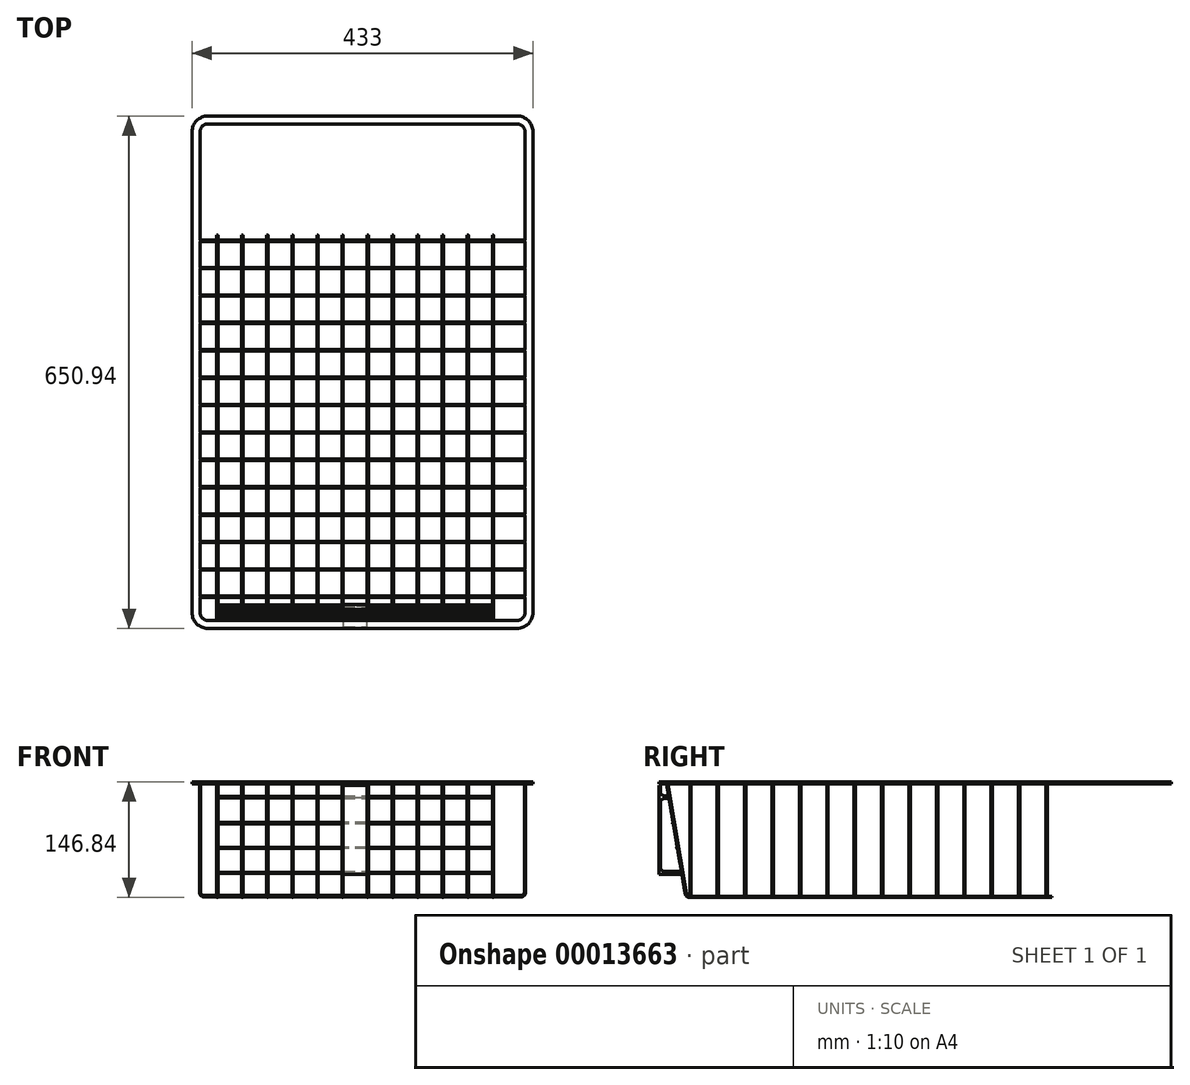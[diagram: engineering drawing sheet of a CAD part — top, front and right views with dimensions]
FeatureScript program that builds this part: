
annotation { "Feature Type Name" : "Feature", "Feature Type Description" : "" }
export const myFeature = defineFeature(function(context is Context, id is Id, definition is map)
    precondition{}
    {
        {
            var Q0;
            Q0=qCreatedBy(makeId("Top.planeOp"),FACE);
            var sketch = newSketch(context, id + "F0", { "sketchPlane" : qUnion([Q0])});
            skCircle(sketch, "E0", {"center": v(-48.63, -32.17) * mm, "radius": 0.85 * mm});
            skCircle(sketch, "E1.0.1.0", {"center": v(-48.63, 2.63) * mm, "radius": 0.85 * mm});
            skCircle(sketch, "E1.0.2.0", {"center": v(-48.63, 37.43) * mm, "radius": 0.85 * mm});
            skCircle(sketch, "E1.0.3.0", {"center": v(-48.63, 72.23) * mm, "radius": 0.85 * mm});
            skCircle(sketch, "E1.0.4.0", {"center": v(-48.63, 107.03) * mm, "radius": 0.85 * mm});
            skCircle(sketch, "E1.0.5.0", {"center": v(-48.63, 141.83) * mm, "radius": 0.85 * mm});
            skCircle(sketch, "E1.0.6.0", {"center": v(-48.63, 176.63) * mm, "radius": 0.85 * mm});
            skCircle(sketch, "E1.0.7.0", {"center": v(-48.63, 211.43) * mm, "radius": 0.85 * mm});
            skCircle(sketch, "E1.0.8.0", {"center": v(-48.63, 246.23) * mm, "radius": 0.85 * mm});
            skCircle(sketch, "E1.0.9.0", {"center": v(-48.63, 281.03) * mm, "radius": 0.85 * mm});
            skCircle(sketch, "E1.0.10.0", {"center": v(-48.63, 315.83) * mm, "radius": 0.85 * mm});
            skCircle(sketch, "E1.0.11.0", {"center": v(-48.63, 350.63) * mm, "radius": 0.85 * mm});
            skCircle(sketch, "E1.0.12.0", {"center": v(-48.63, 385.43) * mm, "radius": 0.85 * mm});
            skCircle(sketch, "E1.0.13.0", {"center": v(-48.63, 420.23) * mm, "radius": 0.85 * mm});
            skLineSegment(sketch, "E1.direction1", {"start": v(-48.63, -32.17) * mm, "end": v(38.17, -32.17) * mm, "construction": true});
            skLineSegment(sketch, "E1.direction2", {"start": v(-48.63, -32.17) * mm, "end": v(-48.63, 2.63) * mm, "construction": true});
            skSolve(sketch);
        }
        {
            var Q0;
            Q0=qCreatedBy(makeId("Front.planeOp"),FACE);
            var sketch = newSketch(context, id + "F1", { "sketchPlane" : qUnion([Q0])});
            skPoint(sketch, "E2.0", {"position": v(-48.63, 0) * mm});
            skLineSegment(sketch, "E3", {"start": v(-48.63, 0) * mm, "end": v(-48.63, -140) * mm});
            skLineSegment(sketch, "E4", {"start": v(-43.63, -145) * mm, "end": v(359.17, -145) * mm});
            skLineSegment(sketch, "E5", {"start": v(364.17, -140) * mm, "end": v(364.17, 0) * mm});
            skPoint(sketch, "E6.visualSharp", {"position": v(-48.63, -145) * mm});
            skArc(sketch, "E6.filletArc", {"start": v(-48.63, -140) * mm, "mid": v(-47.17, -143.54) * mm, "end": v(-43.63, -145) * mm});
            skPoint(sketch, "E7.visualSharp", {"position": v(364.17, -145) * mm});
            skArc(sketch, "E7.filletArc", {"start": v(359.17, -145) * mm, "mid": v(362.7, -143.54) * mm, "end": v(364.17, -140) * mm});
            skCircle(sketch, "E8", {"center": v(-26.63, -145.85) * mm, "radius": 0.85 * mm});
            skLineSegment(sketch, "E9.0", {"start": v(-49.48, 0) * mm, "end": v(-47.78, 0) * mm});
            skCircle(sketch, "E10", {"center": v(-48.63, 0) * mm, "radius": 0.85 * mm, "construction": true});
            skCircle(sketch, "E11.1.0.0", {"center": v(5.2, -145.85) * mm, "radius": 0.85 * mm});
            skCircle(sketch, "E11.2.0.0", {"center": v(37.02, -145.85) * mm, "radius": 0.85 * mm});
            skCircle(sketch, "E11.3.0.0", {"center": v(68.84, -145.85) * mm, "radius": 0.85 * mm});
            skCircle(sketch, "E11.4.0.0", {"center": v(100.67, -145.85) * mm, "radius": 0.85 * mm});
            skCircle(sketch, "E11.5.0.0", {"center": v(132.5, -145.85) * mm, "radius": 0.85 * mm});
            skCircle(sketch, "E11.6.0.0", {"center": v(164.32, -145.85) * mm, "radius": 0.85 * mm});
            skCircle(sketch, "E11.7.0.0", {"center": v(196.14, -145.85) * mm, "radius": 0.85 * mm});
            skCircle(sketch, "E11.8.0.0", {"center": v(227.97, -145.85) * mm, "radius": 0.85 * mm});
            skCircle(sketch, "E11.9.0.0", {"center": v(259.8, -145.85) * mm, "radius": 0.85 * mm});
            skCircle(sketch, "E11.10.0.0", {"center": v(291.62, -145.85) * mm, "radius": 0.85 * mm});
            skCircle(sketch, "E11.11.0.0", {"center": v(323.44, -145.85) * mm, "radius": 0.85 * mm});
            skLineSegment(sketch, "E11.direction1", {"start": v(-26.63, -145.85) * mm, "end": v(5.2, -145.85) * mm, "construction": true});
            skLineSegment(sketch, "E12", {"start": v(-49.48, 0) * mm, "end": v(-49.48, -289.47) * mm, "construction": true});
            skLineSegment(sketch, "E13", {"start": v(133.34, -145) * mm, "end": v(133.34, -145.85) * mm, "construction": true});
            skLineSegment(sketch, "E14", {"start": v(163.47, -145) * mm, "end": v(163.47, -145.85) * mm, "construction": true});
            skSolve(sketch);
        }
        {
            var Q0;
            Q0 = qSketchRegion(id + "F0", true);
            var Q1;
            Q1=sQuery(id+"F1.wireOp",EDGE,"E3");
            var Q2;
            Q2=sQuery(id+"F1.wireOp",EDGE,"E6.filletArc");
            var Q3;
            Q3=sQuery(id+"F1.wireOp",EDGE,"E4");
            var Q4;
            Q4=sQuery(id+"F1.wireOp",EDGE,"E7.filletArc");
            var Q5;
            Q5=sQuery(id+"F1.wireOp",EDGE,"E5");
            sweep(context, id + "F2", {"profiles" : qUnion([Q0]), "path" : qUnion([Q1, Q2, Q3, Q4, Q5])});
        }
        {
            var Q0;
            Q0=qCreatedBy(makeId("Right.planeOp"),FACE);
            var sketch = newSketch(context, id + "F3", { "sketchPlane" : qUnion([Q0])});
            skPoint(sketch, "E15.0", {"position": v(-32.17, 0) * mm});
            skLineSegment(sketch, "E16", {"start": v(-62.17, 0) * mm, "end": v(-38.17, -141.69) * mm});
            skLineSegment(sketch, "E17", {"start": v(-33.24, -145.85) * mm, "end": v(0, -145.85) * mm});
            skPoint(sketch, "E18.visualSharp", {"position": v(-37.46, -145.85) * mm});
            skArc(sketch, "E18.filletArc", {"start": v(-38.17, -141.69) * mm, "mid": v(-36.46, -144.67) * mm, "end": v(-33.24, -145.85) * mm});
            skPoint(sketch, "E19.0", {"position": v(0, -145.85) * mm});
            skCircle(sketch, "E20.0", {"center": v(-32.17, -145) * mm, "radius": 0.85 * mm, "construction": true});
            skLineSegment(sketch, "E21", {"start": v(0, -145.85) * mm, "end": v(427.21, -145.85) * mm});
            skPoint(sketch, "E22", {"position": v(-58.93, -19.08) * mm});
            skLineSegment(sketch, "E23.0", {"start": v(-33.02, 0) * mm, "end": v(-31.32, 0) * mm});
            skCircle(sketch, "E24", {"center": v(-59.77, -19.22) * mm, "radius": 0.85 * mm});
            skLineSegment(sketch, "E25", {"start": v(-31.32, 0) * mm, "end": v(-32.17, 0) * mm, "construction": true});
            skLineSegment(sketch, "E26", {"start": v(-58.93, -19.08) * mm, "end": v(-60.61, -19.36) * mm, "construction": true});
            skLineSegment(sketch, "E27", {"start": v(-63.03, 0) * mm, "end": v(-37.46, -150.94) * mm, "construction": true});
            skCircle(sketch, "E28", {"center": v(-54.17, -52.29) * mm, "radius": 0.85 * mm});
            skCircle(sketch, "E29", {"center": v(-48.86, -83.66) * mm, "radius": 0.85 * mm});
            skCircle(sketch, "E30", {"center": v(-43.47, -115.45) * mm, "radius": 0.85 * mm});
            skSolve(sketch);
        }
        {
            var Q0;
            Q0=makeQuery(id+"F1.imprint","IMPRINT",FACE,{"disambiguationData":[TD([[makeQuery(id+"F1.imprint","IMPRINT",EDGE,{"derivedFrom":sQuery(id+"F1.wireOp",EDGE,"E8")}),1.0]])]});
            var Q1;
            Q1=makeQuery(id+"F1.imprint","IMPRINT",FACE,{"disambiguationData":[TD([[makeQuery(id+"F1.imprint","IMPRINT",EDGE,{"derivedFrom":sQuery(id+"F1.wireOp",EDGE,"E11.1.0.0")}),1.0]])]});
            var Q2;
            Q2=makeQuery(id+"F1.imprint","IMPRINT",FACE,{"disambiguationData":[TD([[makeQuery(id+"F1.imprint","IMPRINT",EDGE,{"derivedFrom":sQuery(id+"F1.wireOp",EDGE,"E11.2.0.0")}),1.0]])]});
            var Q3;
            Q3=makeQuery(id+"F1.imprint","IMPRINT",FACE,{"disambiguationData":[TD([[makeQuery(id+"F1.imprint","IMPRINT",EDGE,{"derivedFrom":sQuery(id+"F1.wireOp",EDGE,"E11.3.0.0")}),1.0]])]});
            var Q4;
            Q4=makeQuery(id+"F1.imprint","IMPRINT",FACE,{"disambiguationData":[TD([[makeQuery(id+"F1.imprint","IMPRINT",EDGE,{"derivedFrom":sQuery(id+"F1.wireOp",EDGE,"E11.4.0.0")}),1.0]])]});
            var Q5;
            Q5=makeQuery(id+"F1.imprint","IMPRINT",FACE,{"disambiguationData":[TD([[makeQuery(id+"F1.imprint","IMPRINT",EDGE,{"derivedFrom":sQuery(id+"F1.wireOp",EDGE,"E11.5.0.0")}),1.0]])]});
            var Q6;
            Q6=makeQuery(id+"F1.imprint","IMPRINT",FACE,{"disambiguationData":[TD([[makeQuery(id+"F1.imprint","IMPRINT",EDGE,{"derivedFrom":sQuery(id+"F1.wireOp",EDGE,"E11.6.0.0")}),1.0]])]});
            var Q7;
            Q7=makeQuery(id+"F1.imprint","IMPRINT",FACE,{"disambiguationData":[TD([[makeQuery(id+"F1.imprint","IMPRINT",EDGE,{"derivedFrom":sQuery(id+"F1.wireOp",EDGE,"E11.7.0.0")}),1.0]])]});
            var Q8;
            Q8=makeQuery(id+"F1.imprint","IMPRINT",FACE,{"disambiguationData":[TD([[makeQuery(id+"F1.imprint","IMPRINT",EDGE,{"derivedFrom":sQuery(id+"F1.wireOp",EDGE,"E11.8.0.0")}),1.0]])]});
            var Q9;
            Q9=makeQuery(id+"F1.imprint","IMPRINT",FACE,{"disambiguationData":[TD([[makeQuery(id+"F1.imprint","IMPRINT",EDGE,{"derivedFrom":sQuery(id+"F1.wireOp",EDGE,"E11.9.0.0")}),1.0]])]});
            var Q10;
            Q10=makeQuery(id+"F1.imprint","IMPRINT",FACE,{"disambiguationData":[TD([[makeQuery(id+"F1.imprint","IMPRINT",EDGE,{"derivedFrom":sQuery(id+"F1.wireOp",EDGE,"E11.10.0.0")}),1.0]])]});
            var Q11;
            Q11=makeQuery(id+"F1.imprint","IMPRINT",FACE,{"disambiguationData":[TD([[makeQuery(id+"F1.imprint","IMPRINT",EDGE,{"derivedFrom":sQuery(id+"F1.wireOp",EDGE,"E11.11.0.0")}),1.0]])]});
            var Q12;
            Q12=sQuery(id+"F3.wireOp",EDGE,"E17");
            var Q13;
            Q13=sQuery(id+"F3.wireOp",EDGE,"E18.filletArc");
            var Q14;
            Q14=sQuery(id+"F3.wireOp",EDGE,"E16");
            sweep(context, id + "F4", {"operationType" : NewBodyOperationType.ADD, "profiles" : qUnion([Q0, Q1, Q2, Q3, Q4, Q5, Q6, Q7, Q8, Q9, Q10, Q11]), "path" : qUnion([Q12, Q13, Q14])});
        }
        {
            var Q0;
            Q0=makeQuery(id+"F1.imprint","IMPRINT",FACE,{"disambiguationData":[TD([[makeQuery(id+"F1.imprint","IMPRINT",EDGE,{"derivedFrom":sQuery(id+"F1.wireOp",EDGE,"E8")}),1.0]])]});
            var Q1;
            Q1=makeQuery(id+"F1.imprint","IMPRINT",FACE,{"disambiguationData":[TD([[makeQuery(id+"F1.imprint","IMPRINT",EDGE,{"derivedFrom":sQuery(id+"F1.wireOp",EDGE,"E11.1.0.0")}),1.0]])]});
            var Q2;
            Q2=makeQuery(id+"F1.imprint","IMPRINT",FACE,{"disambiguationData":[TD([[makeQuery(id+"F1.imprint","IMPRINT",EDGE,{"derivedFrom":sQuery(id+"F1.wireOp",EDGE,"E11.2.0.0")}),1.0]])]});
            var Q3;
            Q3=makeQuery(id+"F1.imprint","IMPRINT",FACE,{"disambiguationData":[TD([[makeQuery(id+"F1.imprint","IMPRINT",EDGE,{"derivedFrom":sQuery(id+"F1.wireOp",EDGE,"E11.3.0.0")}),1.0]])]});
            var Q4;
            Q4=makeQuery(id+"F1.imprint","IMPRINT",FACE,{"disambiguationData":[TD([[makeQuery(id+"F1.imprint","IMPRINT",EDGE,{"derivedFrom":sQuery(id+"F1.wireOp",EDGE,"E11.4.0.0")}),1.0]])]});
            var Q5;
            Q5=makeQuery(id+"F1.imprint","IMPRINT",FACE,{"disambiguationData":[TD([[makeQuery(id+"F1.imprint","IMPRINT",EDGE,{"derivedFrom":sQuery(id+"F1.wireOp",EDGE,"E11.5.0.0")}),1.0]])]});
            var Q6;
            Q6=makeQuery(id+"F1.imprint","IMPRINT",FACE,{"disambiguationData":[TD([[makeQuery(id+"F1.imprint","IMPRINT",EDGE,{"derivedFrom":sQuery(id+"F1.wireOp",EDGE,"E11.6.0.0")}),1.0]])]});
            var Q7;
            Q7=makeQuery(id+"F1.imprint","IMPRINT",FACE,{"disambiguationData":[TD([[makeQuery(id+"F1.imprint","IMPRINT",EDGE,{"derivedFrom":sQuery(id+"F1.wireOp",EDGE,"E11.7.0.0")}),1.0]])]});
            var Q8;
            Q8=makeQuery(id+"F1.imprint","IMPRINT",FACE,{"disambiguationData":[TD([[makeQuery(id+"F1.imprint","IMPRINT",EDGE,{"derivedFrom":sQuery(id+"F1.wireOp",EDGE,"E11.8.0.0")}),1.0]])]});
            var Q9;
            Q9=makeQuery(id+"F1.imprint","IMPRINT",FACE,{"disambiguationData":[TD([[makeQuery(id+"F1.imprint","IMPRINT",EDGE,{"derivedFrom":sQuery(id+"F1.wireOp",EDGE,"E11.9.0.0")}),1.0]])]});
            var Q10;
            Q10=makeQuery(id+"F1.imprint","IMPRINT",FACE,{"disambiguationData":[TD([[makeQuery(id+"F1.imprint","IMPRINT",EDGE,{"derivedFrom":sQuery(id+"F1.wireOp",EDGE,"E11.10.0.0")}),1.0]])]});
            var Q11;
            Q11=makeQuery(id+"F1.imprint","IMPRINT",FACE,{"disambiguationData":[TD([[makeQuery(id+"F1.imprint","IMPRINT",EDGE,{"derivedFrom":sQuery(id+"F1.wireOp",EDGE,"E11.11.0.0")}),1.0]])]});
            var Q12;
            Q12=sQuery(id+"F3.wireOp",EDGE,"E21");
            sweep(context, id + "F5", {"operationType" : NewBodyOperationType.ADD, "profiles" : qUnion([Q0, Q1, Q2, Q3, Q4, Q5, Q6, Q7, Q8, Q9, Q10, Q11]), "path" : qUnion([Q12])});
        }
        {
            var Q0;
            Q0=qCreatedBy(makeId("Top.planeOp"),FACE);
            var sketch = newSketch(context, id + "F6", { "sketchPlane" : qUnion([Q0])});
            skLineSegment(sketch, "E31.bottom", {"start": v(-38.63, -62.17) * mm, "end": v(354.17, -62.17) * mm});
            skLineSegment(sketch, "E31.top", {"start": v(-38.63, 568.57) * mm, "end": v(354.17, 568.57) * mm});
            skLineSegment(sketch, "E31.left", {"start": v(-48.63, -52.17) * mm, "end": v(-48.63, 558.57) * mm});
            skLineSegment(sketch, "E31.right", {"start": v(364.17, -52.17) * mm, "end": v(364.17, 558.57) * mm});
            skPoint(sketch, "E32.visualSharp", {"position": v(-48.63, 568.57) * mm});
            skArc(sketch, "E32.filletArc", {"start": v(-38.63, 568.57) * mm, "mid": v(-45.7, 565.64) * mm, "end": v(-48.63, 558.57) * mm});
            skPoint(sketch, "E33.visualSharp", {"position": v(364.17, 568.57) * mm});
            skArc(sketch, "E33.filletArc", {"start": v(364.17, 558.57) * mm, "mid": v(361.24, 565.64) * mm, "end": v(354.17, 568.57) * mm});
            skPoint(sketch, "E34.visualSharp", {"position": v(364.17, -62.17) * mm});
            skArc(sketch, "E34.filletArc", {"start": v(354.17, -62.17) * mm, "mid": v(361.24, -59.24) * mm, "end": v(364.17, -52.17) * mm});
            skPoint(sketch, "E35.visualSharp", {"position": v(-48.63, -62.17) * mm});
            skArc(sketch, "E35.filletArc", {"start": v(-48.63, -52.17) * mm, "mid": v(-45.7, -59.24) * mm, "end": v(-38.63, -62.17) * mm});
            skArc(sketch, "E36.0", {"start": v(-38.63, 578.67) * mm, "mid": v(-52.84, 572.78) * mm, "end": v(-58.73, 558.57) * mm});
            skLineSegment(sketch, "E36.1", {"start": v(-58.73, -52.17) * mm, "end": v(-58.73, 558.57) * mm});
            skArc(sketch, "E36.2", {"start": v(-58.73, -52.17) * mm, "mid": v(-52.84, -66.38) * mm, "end": v(-38.63, -72.27) * mm});
            skLineSegment(sketch, "E36.3", {"start": v(-38.63, -72.27) * mm, "end": v(354.17, -72.27) * mm});
            skArc(sketch, "E36.4", {"start": v(354.17, -72.27) * mm, "mid": v(368.38, -66.38) * mm, "end": v(374.27, -52.17) * mm});
            skLineSegment(sketch, "E36.5", {"start": v(-38.63, 578.67) * mm, "end": v(354.17, 578.67) * mm});
            skLineSegment(sketch, "E36.6", {"start": v(374.27, -52.17) * mm, "end": v(374.27, 558.57) * mm});
            skArc(sketch, "E36.7", {"start": v(374.27, 558.57) * mm, "mid": v(368.38, 572.78) * mm, "end": v(354.17, 578.67) * mm});
            skSolve(sketch);
        }
        {
            var Q0;
            Q0=makeQuery(id+"F6.imprint","IMPRINT",FACE,{"disambiguationData":[TD([[makeQuery(id+"F6.imprint","IMPRINT",EDGE,{"derivedFrom":sQuery(id+"F6.wireOp",EDGE,"E31.bottom")}),-1.0]])]});
            extrude(context, id + "F7", {"entities" : qUnion([Q0]), "operationType" : NewBodyOperationType.ADD, "oppositeDirection" : true, "depth" : 2.15 * mm});
        }
        {
            var Q0;
            Q0=qCreatedBy(makeId("Right.planeOp"),FACE);
            var Q1;
            Q1=sQuery(id+"F1.wireOp",VERTEX,"E11.11.0.0.center");
            cPlane(context, id + "F8", {"entities" : qUnion([Q0, Q1]), "cplaneType" : CPlaneType.PLANE_POINT, "offset" : 150 * mm, "width" : 150 * mm, "height" : 150 * mm});
        }
        {
            var Q0;
            Q0=qCreatedBy(makeId("Right.planeOp"),FACE);
            var Q1;
            Q1=sQuery(id+"F1.wireOp",VERTEX,"E8.center");
            cPlane(context, id + "F9", {"entities" : qUnion([Q0, Q1]), "cplaneType" : CPlaneType.PLANE_POINT, "offset" : 150 * mm, "width" : 150 * mm, "height" : 150 * mm});
        }
        {
            var Q0;
            Q0=makeQuery(id+"F3.imprint","IMPRINT",FACE,{"disambiguationData":[TD([[makeQuery(id+"F3.imprint","IMPRINT",EDGE,{"derivedFrom":sQuery(id+"F3.wireOp",EDGE,"E24")}),1.0]])]});
            var Q1;
            Q1=makeQuery(id+"F3.imprint","IMPRINT",FACE,{"disambiguationData":[TD([[makeQuery(id+"F3.imprint","IMPRINT",EDGE,{"derivedFrom":sQuery(id+"F3.wireOp",EDGE,"E28")}),1.0]])]});
            var Q2;
            Q2=makeQuery(id+"F3.imprint","IMPRINT",FACE,{"disambiguationData":[TD([[makeQuery(id+"F3.imprint","IMPRINT",EDGE,{"derivedFrom":sQuery(id+"F3.wireOp",EDGE,"E29")}),1.0]])]});
            var Q3;
            Q3=makeQuery(id+"F3.imprint","IMPRINT",FACE,{"disambiguationData":[TD([[makeQuery(id+"F3.imprint","IMPRINT",EDGE,{"derivedFrom":sQuery(id+"F3.wireOp",EDGE,"E30")}),1.0]])]});
            var Q4;
            Q4=qCreatedBy(id+"F8.planeOp",FACE);
            extrude(context, id + "F10", {"entities" : qUnion([Q0, Q1, Q2, Q3]), "operationType" : NewBodyOperationType.ADD, "endBound" : BoundingType.UP_TO_SURFACE, "endBoundEntityFace" : qUnion([Q4]), "depth" : 25 * mm});
        }
        {
            var Q0;
            Q0=makeQuery(id+"F3.imprint","IMPRINT",FACE,{"disambiguationData":[TD([[makeQuery(id+"F3.imprint","IMPRINT",EDGE,{"derivedFrom":sQuery(id+"F3.wireOp",EDGE,"E24")}),1.0]])]});
            var Q1;
            Q1=makeQuery(id+"F3.imprint","IMPRINT",FACE,{"disambiguationData":[TD([[makeQuery(id+"F3.imprint","IMPRINT",EDGE,{"derivedFrom":sQuery(id+"F3.wireOp",EDGE,"E28")}),1.0]])]});
            var Q2;
            Q2=makeQuery(id+"F3.imprint","IMPRINT",FACE,{"disambiguationData":[TD([[makeQuery(id+"F3.imprint","IMPRINT",EDGE,{"derivedFrom":sQuery(id+"F3.wireOp",EDGE,"E29")}),1.0]])]});
            var Q3;
            Q3=makeQuery(id+"F3.imprint","IMPRINT",FACE,{"disambiguationData":[TD([[makeQuery(id+"F3.imprint","IMPRINT",EDGE,{"derivedFrom":sQuery(id+"F3.wireOp",EDGE,"E30")}),1.0]])]});
            var Q4;
            Q4=qCreatedBy(id+"F9.planeOp",FACE);
            extrude(context, id + "F11", {"entities" : qUnion([Q0, Q1, Q2, Q3]), "operationType" : NewBodyOperationType.ADD, "endBound" : BoundingType.UP_TO_SURFACE, "oppositeDirection" : true, "endBoundEntityFace" : qUnion([Q4]), "depth" : 25 * mm});
        }
        {
            var Q0;
            Q0=qCreatedBy(makeId("Right.planeOp"),FACE);
            var Q1;
            Q1=sQuery(id+"F1.wireOp",VERTEX,"E14.end");
            cPlane(context, id + "F12", {"entities" : qUnion([Q0, Q1]), "cplaneType" : CPlaneType.PLANE_POINT, "offset" : 150 * mm, "width" : 150 * mm, "height" : 150 * mm});
        }
        {
            var Q0;
            Q0=qCreatedBy(makeId("Right.planeOp"),FACE);
            var Q1;
            Q1=sQuery(id+"F1.wireOp",VERTEX,"E13.end");
            cPlane(context, id + "F13", {"entities" : qUnion([Q0, Q1]), "cplaneType" : CPlaneType.PLANE_POINT, "offset" : 150 * mm, "width" : 150 * mm, "height" : 150 * mm});
        }
        {
            var Q0;
            Q0=qCreatedBy(id+"F12.planeOp",FACE);
            var sketch = newSketch(context, id + "F14", { "sketchPlane" : qUnion([Q0])});
            skCircle(sketch, "E37.0", {"center": v(-43.47, -115.45) * mm, "radius": 0.85 * mm});
            skCircle(sketch, "E38.0", {"center": v(-48.86, -83.66) * mm, "radius": 0.85 * mm});
            skCircle(sketch, "E39.0", {"center": v(-54.17, -52.29) * mm, "radius": 0.85 * mm});
            skCircle(sketch, "E40.0", {"center": v(-59.77, -19.22) * mm, "radius": 0.85 * mm});
            skLineSegment(sketch, "E41.0.1", {"start": v(-72.27, 0) * mm, "end": v(-72.27, -2.15) * mm, "construction": true});
            skLineSegment(sketch, "E41.0.3", {"start": v(-72.27, -2.15) * mm, "end": v(-72.27, 0) * mm, "construction": true});
            skLineSegment(sketch, "E42", {"start": v(-61.3, 0) * mm, "end": v(-37.23, -142.14) * mm, "construction": true});
            skLineSegment(sketch, "E43", {"start": v(-39, -141.83) * mm, "end": v(-62.66, -2.15) * mm, "construction": true});
            skLineSegment(sketch, "E44", {"start": v(-61.3, 0) * mm, "end": v(-72.27, 0) * mm, "construction": true});
            skLineSegment(sketch, "E45", {"start": v(-62.66, -2.15) * mm, "end": v(-72.27, -2.15) * mm, "construction": true});
            skLineSegment(sketch, "E46.bottom", {"start": v(-72.27, -2.15) * mm, "end": v(-70.27, -2.15) * mm});
            skLineSegment(sketch, "E46.top", {"start": v(-72.27, -117.3) * mm, "end": v(-70.27, -117.3) * mm});
            skLineSegment(sketch, "E46.left", {"start": v(-72.27, -2.15) * mm, "end": v(-72.27, -117.3) * mm});
            skLineSegment(sketch, "E46.right", {"start": v(-70.27, -2.15) * mm, "end": v(-70.27, -117.3) * mm});
            skPoint(sketch, "E47.0", {"position": v(-33.24, -145.85) * mm});
            skLineSegment(sketch, "E48.bottom", {"start": v(-70.27, -17.37) * mm, "end": v(-59.77, -17.37) * mm});
            skArc(sketch, "E49", {"start": v(-59.22, -20.99) * mm, "mid": v(-59.61, -17.38) * mm, "end": v(-60.62, -20.86) * mm});
            skLineSegment(sketch, "E50", {"start": v(-70.27, -21.07) * mm, "end": v(-60.62, -21.07) * mm});
            skLineSegment(sketch, "E51", {"start": v(-60.62, -21.07) * mm, "end": v(-60.62, -19.22) * mm});
            skLineSegment(sketch, "E52", {"start": v(-59.22, -19.87) * mm, "end": v(-59.22, -20.99) * mm});
            skLineSegment(sketch, "E53.bottom", {"start": v(-70.27, -113.6) * mm, "end": v(-43.47, -113.6) * mm});
            skLineSegment(sketch, "E53.top", {"start": v(-70.27, -117.3) * mm, "end": v(-44.32, -117.3) * mm});
            skLineSegment(sketch, "E53.left", {"start": v(-70.27, -113.6) * mm, "end": v(-70.27, -117.3) * mm});
            skArc(sketch, "E54", {"start": v(-44.02, -117.21) * mm, "mid": v(-43.6, -117.3) * mm, "end": v(-43.16, -117.27) * mm});
            skLineSegment(sketch, "E55", {"start": v(-42.92, -116.1) * mm, "end": v(-42.92, -117.21) * mm});
            skLineSegment(sketch, "E56", {"start": v(-59.22, -20.43) * mm, "end": v(-60.62, -20.43) * mm, "construction": true});
            skLineSegment(sketch, "E57", {"start": v(-44.32, -115.45) * mm, "end": v(-44.32, -117.3) * mm});
            skLineSegment(sketch, "E58", {"start": v(-42.92, -116.65) * mm, "end": v(-44.32, -116.65) * mm, "construction": true});
            skArc(sketch, "E59.trimOffspring", {"start": v(-42.92, -117.21) * mm, "mid": v(-43.31, -113.6) * mm, "end": v(-44.32, -117.09) * mm});
            skLineSegment(sketch, "E60", {"start": v(-70.27, -4.15) * mm, "end": v(-72.27, -4.15) * mm});
            skSolve(sketch);
        }
        {
            var Q0;
            {var subQ4=sQuery(id+"F14.wireOp",EDGE,"E48.bottom");Q0=makeQuery(id+"F14.imprint","IMPRINT",FACE,{"disambiguationData":[TD([[makeQuery(id+"F14.imprint","IMPRINT",EDGE,{"derivedFrom":subQ4}),-1.0]])]});}
            var Q1;
            {var subQ0=sQuery(id+"F14.wireOp",EDGE,"E52");Q1=makeQuery(id+"F14.imprint","IMPRINT",FACE,{"disambiguationData":[TD([[makeQuery(id+"F14.imprint","IMPRINT",EDGE,{"derivedFrom":subQ0}),1.0]])]});}
            var Q2;
            {var subQ3=sQuery(id+"F14.wireOp",EDGE,"E53.bottom");Q2=makeQuery(id+"F14.imprint","IMPRINT",FACE,{"disambiguationData":[TD([[makeQuery(id+"F14.imprint","IMPRINT",EDGE,{"derivedFrom":subQ3}),-1.0]])]});}
            var Q3;
            {var subQ4=sQuery(id+"F14.wireOp",EDGE,"E55");Q3=makeQuery(id+"F14.imprint","IMPRINT",FACE,{"disambiguationData":[TD([[makeQuery(id+"F14.imprint","IMPRINT",EDGE,{"derivedFrom":subQ4}),1.0]])]});}
            var Q4;
            {var subQ6=sQuery(id+"F14.wireOp",EDGE,"E46.top");Q4=makeQuery(id+"F14.imprint","IMPRINT",FACE,{"disambiguationData":[TD([[makeQuery(id+"F14.imprint","IMPRINT",EDGE,{"derivedFrom":subQ6}),1.0]])]});}
            var Q5;
            Q5=qCreatedBy(id+"F13.planeOp",FACE);
            extrude(context, id + "F15", {"entities" : qUnion([Q0, Q1, Q2, Q3, Q4]), "endBound" : BoundingType.UP_TO_SURFACE, "oppositeDirection" : true, "endBoundEntityFace" : qUnion([Q5]), "depth" : 25 * mm});
        }
        {
            var Q0;
            Q0=makeQuery(id+"F15.opExtrude","SWEPT_EDGE",EDGE,{"disambiguationData":[OSD([sQuery(id+"F14.wireOp",EDGE,"E46.right"),sQuery(id+"F14.wireOp",EDGE,"E48.bottom")])]});
            var Q1;
            Q1=makeQuery(id+"F15.opExtrude","SWEPT_EDGE",EDGE,{"disambiguationData":[OSD([sQuery(id+"F14.wireOp",EDGE,"E46.right"),sQuery(id+"F14.wireOp",EDGE,"E50")])]});
            var Q2;
            Q2=makeQuery(id+"F15.opExtrude","SWEPT_EDGE",EDGE,{"disambiguationData":[OSD([sQuery(id+"F14.wireOp",EDGE,"E46.right"),sQuery(id+"F14.wireOp",EDGE,"E53.bottom"),sQuery(id+"F14.wireOp",EDGE,"E53.left")])]});
            fillet(context, id + "F16", {"entities" : qUnion([Q0, Q1, Q2]), "radius" : 5 * mm, "tangentPropagation" : true, "allowEdgeOverflow" : false});
        }
    });
